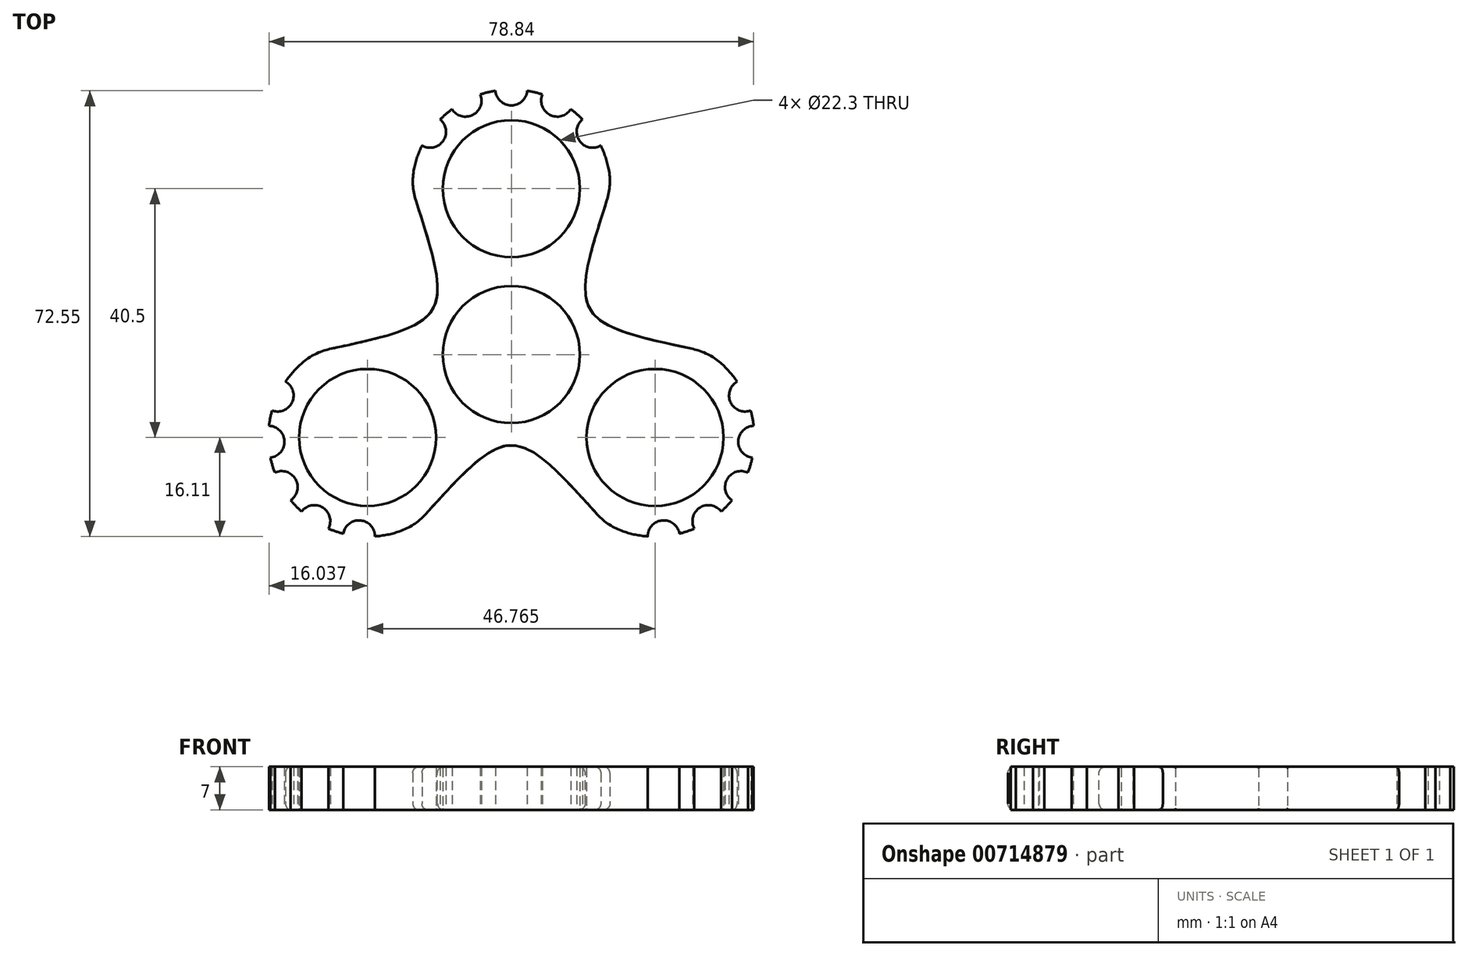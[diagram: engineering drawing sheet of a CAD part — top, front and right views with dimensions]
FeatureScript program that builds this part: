
annotation { "Feature Type Name" : "Feature", "Feature Type Description" : "" }
export const myFeature = defineFeature(function(context is Context, id is Id, definition is map)
    precondition{}
    {
        {
            var Q0;
            Q0=qCreatedBy(makeId("Top.planeOp"),FACE);
            var sketch = newSketch(context, id + "F0", { "sketchPlane" : qUnion([Q0])});
            skCircle(sketch, "E0", {"center": v(0, 0) * mm, "radius": 11.15 * mm});
            skLineSegment(sketch, "E1.0", {"start": v(-15.15, 0) * mm, "end": v(-15.15, 0) * mm});
            skLineSegment(sketch, "E2", {"start": v(0, 0) * mm, "end": v(0, 27) * mm, "construction": true});
            skCircle(sketch, "E3", {"center": v(0, 27) * mm, "radius": 11.15 * mm});
            skArc(sketch, "E4.0", {"start": v(16.15, 27) * mm, "mid": v(0, 43.15) * mm, "end": v(-16.15, 27) * mm});
            skLineSegment(sketch, "E5", {"start": v(-15.15, 0) * mm, "end": v(15.15, 0) * mm, "construction": true});
            skLineSegment(sketch, "E6", {"start": v(-16.15, 27) * mm, "end": v(16.15, 27) * mm, "construction": true});
            skPoint(sketch, "E7.trimOffspring.end.orphan", {"position": v(-15.15, 0) * mm});
            skLineSegment(sketch, "E8", {"start": v(-16.15, 27) * mm, "end": v(-16.15, 27) * mm});
            skArc(sketch, "E9.trimOffspring", {"start": v(-15.15, 0) * mm, "mid": v(0, -15.15) * mm, "end": v(15.15, 0) * mm, "construction": true});
            skLineSegment(sketch, "E10.trimOffspring", {"start": v(16.15, 27) * mm, "end": v(16.15, 27) * mm});
            skCircle(sketch, "E11", {"center": v(0, 43.15) * mm, "radius": 2.6 * mm});
            skCircle(sketch, "E12.1.0", {"center": v(7.46, 41.33) * mm, "radius": 2.6 * mm});
            skCircle(sketch, "E12.2.0", {"center": v(13.23, 36.26) * mm, "radius": 2.6 * mm});
            skLineSegment(sketch, "E12.anchor1", {"start": v(0, 27) * mm, "end": v(0, 43.15) * mm, "construction": true});
            skLineSegment(sketch, "E12.anchor2", {"start": v(0, 27) * mm, "end": v(13.23, 36.26) * mm, "construction": true});
            skCircle(sketch, "E13.MirrorC", {"center": v(-7.46, 41.33) * mm, "radius": 2.6 * mm});
            skCircle(sketch, "E14.MirrorC", {"center": v(-13.23, 36.26) * mm, "radius": 2.6 * mm});
            skLineSegment(sketch, "E15.1.0", {"start": v(7.57, -13.12) * mm, "end": v(-7.58, 13.12) * mm, "construction": true});
            skCircle(sketch, "E15.1.1", {"center": v(-38.02, -6.67) * mm, "radius": 2.6 * mm});
            skLineSegment(sketch, "E15.1.2", {"start": v(0, 0) * mm, "end": v(-23.38, -13.5) * mm, "construction": true});
            skLineSegment(sketch, "E15.1.3", {"start": v(-23.38, -13.5) * mm, "end": v(-38.02, -6.67) * mm, "construction": true});
            skLineSegment(sketch, "E15.1.4", {"start": v(-15.3, -27.49) * mm, "end": v(-31.46, 0.49) * mm, "construction": true});
            skCircle(sketch, "E15.1.5", {"center": v(-23.38, -13.5) * mm, "radius": 11.15 * mm});
            skCircle(sketch, "E15.1.6", {"center": v(-24.8, -29.59) * mm, "radius": 2.6 * mm});
            skCircle(sketch, "E15.1.7", {"center": v(-32.06, -27.12) * mm, "radius": 2.6 * mm});
            skLineSegment(sketch, "E15.1.8", {"start": v(-23.38, -13.5) * mm, "end": v(-37.37, -21.57) * mm, "construction": true});
            skPoint(sketch, "E15.1.9", {"position": v(7.57, -13.12) * mm});
            skCircle(sketch, "E15.1.11", {"center": v(-39.52, -14.2) * mm, "radius": 2.6 * mm});
            skCircle(sketch, "E15.1.13", {"center": v(-37.37, -21.57) * mm, "radius": 2.6 * mm});
            skArc(sketch, "E15.1.14", {"start": v(-31.46, 0.49) * mm, "mid": v(-37.37, -21.57) * mm, "end": v(-15.3, -27.49) * mm});
            skPoint(sketch, "E15.1.15", {"position": v(-23.38, -13.5) * mm});
            skLineSegment(sketch, "E15.2.0", {"start": v(7.57, 13.12) * mm, "end": v(-7.58, -13.12) * mm, "construction": true});
            skCircle(sketch, "E15.2.1", {"center": v(24.8, -29.59) * mm, "radius": 2.6 * mm});
            skLineSegment(sketch, "E15.2.2", {"start": v(0, 0) * mm, "end": v(23.38, -13.5) * mm, "construction": true});
            skLineSegment(sketch, "E15.2.3", {"start": v(23.38, -13.5) * mm, "end": v(24.8, -29.59) * mm, "construction": true});
            skLineSegment(sketch, "E15.2.4", {"start": v(31.46, 0.49) * mm, "end": v(15.3, -27.49) * mm, "construction": true});
            skCircle(sketch, "E15.2.5", {"center": v(23.38, -13.5) * mm, "radius": 11.15 * mm});
            skCircle(sketch, "E15.2.6", {"center": v(38.02, -6.67) * mm, "radius": 2.6 * mm});
            skCircle(sketch, "E15.2.7", {"center": v(39.52, -14.2) * mm, "radius": 2.6 * mm});
            skLineSegment(sketch, "E15.2.8", {"start": v(23.38, -13.5) * mm, "end": v(37.37, -21.57) * mm, "construction": true});
            skCircle(sketch, "E15.2.11", {"center": v(32.06, -27.12) * mm, "radius": 2.6 * mm});
            skArc(sketch, "E15.2.12", {"start": v(7.57, 13.12) * mm, "mid": v(-13.12, 7.57) * mm, "end": v(-7.58, -13.12) * mm, "construction": true});
            skCircle(sketch, "E15.2.13", {"center": v(37.37, -21.57) * mm, "radius": 2.6 * mm});
            skArc(sketch, "E15.2.14", {"start": v(15.3, -27.49) * mm, "mid": v(37.37, -21.57) * mm, "end": v(31.46, 0.49) * mm});
            skPoint(sketch, "E15.2.15", {"position": v(23.38, -13.5) * mm});
            skFitSpline(sketch, "E16", {"points": [v(16.15, 27) * mm, v(31.46, 0.49) * mm], "startDerivative": vector(-21.08, -65.2) * mm, "endDerivative": vector(67, -14.34) * mm});
            skLineSegment(sketch, "E17", {"start": v(0, 0) * mm, "end": v(26.97, 15.57) * mm, "construction": true});
            skLineSegment(sketch, "E18", {"start": v(-15.3, -27.49) * mm, "end": v(-3.01, -11.46) * mm});
            skLineSegment(sketch, "E19", {"start": v(-3.01, -11.46) * mm, "end": v(3.36, -11.46) * mm});
            skLineSegment(sketch, "E20", {"start": v(3.36, -11.46) * mm, "end": v(15.3, -27.49) * mm});
            skLineSegment(sketch, "E21", {"start": v(-31.46, 0.49) * mm, "end": v(-13.47, 2.14) * mm});
            skLineSegment(sketch, "E22", {"start": v(-13.47, 2.14) * mm, "end": v(-9.18, 9.2) * mm});
            skLineSegment(sketch, "E23", {"start": v(-9.18, 9.2) * mm, "end": v(-16.15, 27) * mm});
            skSolve(sketch);
        }
        {
            var Q0;
            Q0=qCreatedBy(makeId("Right.planeOp"),FACE);
            var sketch = newSketch(context, id + "F1", { "sketchPlane" : qUnion([Q0])});
            skLineSegment(sketch, "E24", {"start": v(0, 18.91) * mm, "end": v(0, -18.72) * mm, "construction": true});
            skSolve(sketch);
        }
        {
            var Q0;
            Q0=makeQuery(id+"F0.imprint","IMPRINT",FACE,{"disambiguationData":[TD([[makeQuery(id+"F0.imprint","IMPRINT",EDGE,{"derivedFrom":sQuery(id+"F0.wireOp",EDGE,"E0")}),-1.0]])]});
            var Q1;
            Q1=makeQuery(id+"F0.imprint","IMPRINT",FACE,{"disambiguationData":[TD([[makeQuery(id+"F0.imprint","IMPRINT",EDGE,{"derivedFrom":sQuery(id+"F0.wireOp",EDGE,"E3")}),-1.0]])]});
            extrude(context, id + "F2", {"entities" : qUnion([Q0, Q1]), "depth" : 7 * mm, "offsetDistance" : 25 * mm});
        }
        {
            var Q0;
            Q0=makeQuery(id+"F2.opExtrude","SWEPT_BODY",BODY,{"disambiguationData":[OSD([sQuery(id+"F0.wireOp",EDGE,"E0"),sQuery(id+"F0.wireOp",EDGE,"E1.0"),sQuery(id+"F0.wireOp",EDGE,"E3"),sQuery(id+"F0.wireOp",EDGE,"E4.0"),sQuery(id+"F0.wireOp",EDGE,"oIW5whhO-fQ4n-saJ2-gWf4-q0JPziCMkqRt"),sQuery(id+"F0.wireOp",EDGE,"e7664bf7-e720-472f-93c8-efa73fce652a0.MirrorCS"),sQuery(id+"F0.wireOp",EDGE,"15db0cb3-5bd8-46cc-a881-ea2e00802e11.filletArc"),sQuery(id+"F0.wireOp",EDGE,"163ba6b5-26b9-4c58-8659-ca6763b85cf9.filletArc")])]});
            var Q1;
            Q1=sQuery(id+"F1.wireOp",EDGE,"E24");
            circularPattern(context, id + "F3", {"operationType" : NewBodyOperationType.ADD, "entities" : qUnion([Q0]), "axis" : qUnion([Q1]), "angle" : 360 * degree, "instanceCount" : 3, "equalSpace" : true});
        }
        {
            var Q0;
            Q0=makeQuery(id+"F2.opExtrude","SWEPT_EDGE",EDGE,{"disambiguationData":[OSD([sQuery(id+"F0.wireOp",EDGE,"E4.0"),sQuery(id+"F0.wireOp",EDGE,"E16")])]});
            var Q1;
            Q1=makeQuery(id+"F2.opExtrude","SWEPT_EDGE",EDGE,{"disambiguationData":[OSD([sQuery(id+"F0.wireOp",EDGE,"E15.2.14"),sQuery(id+"F0.wireOp",EDGE,"E16")])]});
            var Q2;
            Q2=makeQuery(id+"F3.boolean.opBoolean","MERGE",EDGE,{"derivedFrom":[makeQuery(id+"F2.opExtrude","SWEPT_EDGE",EDGE,{"disambiguationData":[OSD([sQuery(id+"F0.wireOp",EDGE,"E15.2.14"),sQuery(id+"F0.wireOp",EDGE,"E20")])]}),makeQuery(id+"F3.opPattern","COPY",EDGE,{"derivedFrom":makeQuery(id+"F2.opExtrude","SWEPT_EDGE",EDGE,{"disambiguationData":[OSD([sQuery(id+"F0.wireOp",EDGE,"E4.0"),sQuery(id+"F0.wireOp",EDGE,"E16")])]}),"instanceName":"1"})]});
            var Q3;
            Q3=makeQuery(id+"F3.boolean.opBoolean","MERGE",EDGE,{"derivedFrom":[makeQuery(id+"F2.opExtrude","SWEPT_EDGE",EDGE,{"disambiguationData":[OSD([sQuery(id+"F0.wireOp",EDGE,"E15.1.14"),sQuery(id+"F0.wireOp",EDGE,"E18")])]}),makeQuery(id+"F3.opPattern","COPY",EDGE,{"derivedFrom":makeQuery(id+"F2.opExtrude","SWEPT_EDGE",EDGE,{"disambiguationData":[OSD([sQuery(id+"F0.wireOp",EDGE,"E15.2.14"),sQuery(id+"F0.wireOp",EDGE,"E16")])]}),"instanceName":"1"})]});
            var Q4;
            Q4=makeQuery(id+"F3.boolean.opBoolean","MERGE",EDGE,{"derivedFrom":[makeQuery(id+"F2.opExtrude","SWEPT_EDGE",EDGE,{"disambiguationData":[OSD([sQuery(id+"F0.wireOp",EDGE,"E15.1.14"),sQuery(id+"F0.wireOp",EDGE,"E21")])]}),makeQuery(id+"F3.opPattern","COPY",EDGE,{"derivedFrom":makeQuery(id+"F2.opExtrude","SWEPT_EDGE",EDGE,{"disambiguationData":[OSD([sQuery(id+"F0.wireOp",EDGE,"E15.2.14"),sQuery(id+"F0.wireOp",EDGE,"E20")])]}),"instanceName":"1"}),makeQuery(id+"F3.opPattern","COPY",EDGE,{"derivedFrom":makeQuery(id+"F2.opExtrude","SWEPT_EDGE",EDGE,{"disambiguationData":[OSD([sQuery(id+"F0.wireOp",EDGE,"E4.0"),sQuery(id+"F0.wireOp",EDGE,"E16")])]}),"instanceName":"2"})]});
            var Q5;
            Q5=makeQuery(id+"F3.boolean.opBoolean","MERGE",EDGE,{"derivedFrom":[makeQuery(id+"F2.opExtrude","SWEPT_EDGE",EDGE,{"disambiguationData":[OSD([sQuery(id+"F0.wireOp",EDGE,"E4.0"),sQuery(id+"F0.wireOp",EDGE,"E23")])]}),makeQuery(id+"F3.opPattern","COPY",EDGE,{"derivedFrom":makeQuery(id+"F2.opExtrude","SWEPT_EDGE",EDGE,{"disambiguationData":[OSD([sQuery(id+"F0.wireOp",EDGE,"E15.1.14"),sQuery(id+"F0.wireOp",EDGE,"E18")])]}),"instanceName":"1"}),makeQuery(id+"F3.opPattern","COPY",EDGE,{"derivedFrom":makeQuery(id+"F2.opExtrude","SWEPT_EDGE",EDGE,{"disambiguationData":[OSD([sQuery(id+"F0.wireOp",EDGE,"E15.2.14"),sQuery(id+"F0.wireOp",EDGE,"E16")])]}),"instanceName":"2"})]});
            fillet(context, id + "F4", {"entities" : qUnion([Q0, Q1, Q2, Q3, Q4, Q5]), "radius" : 10 * mm, "tangentPropagation" : true, "allowEdgeOverflow" : false});
        }
        {
            var Q0;
            Q0=makeQuery(id+"F2.opExtrude","CAP_EDGE",EDGE,{"disambiguationData":[OSD([sQuery(id+"F0.wireOp",EDGE,"E16")])],"isStart":false});
            var Q1;
            Q1=makeQuery(id+"F3.opPattern","COPY",EDGE,{"derivedFrom":makeQuery(id+"F2.opExtrude","CAP_EDGE",EDGE,{"disambiguationData":[OSD([sQuery(id+"F0.wireOp",EDGE,"E16")])],"isStart":false}),"instanceName":"2"});
            var Q2;
            Q2=makeQuery(id+"F3.opPattern","COPY",EDGE,{"derivedFrom":makeQuery(id+"F2.opExtrude","CAP_EDGE",EDGE,{"disambiguationData":[OSD([sQuery(id+"F0.wireOp",EDGE,"E16")])],"isStart":false}),"instanceName":"1"});
            var Q3;
            Q3=makeQuery(id+"F3.opPattern","COPY",EDGE,{"derivedFrom":makeQuery(id+"F2.opExtrude","CAP_EDGE",EDGE,{"disambiguationData":[OSD([sQuery(id+"F0.wireOp",EDGE,"E16")])],"isStart":true}),"instanceName":"1"});
            var Q4;
            Q4=makeQuery(id+"F3.opPattern","COPY",EDGE,{"derivedFrom":makeQuery(id+"F2.opExtrude","CAP_EDGE",EDGE,{"disambiguationData":[OSD([sQuery(id+"F0.wireOp",EDGE,"E16")])],"isStart":true}),"instanceName":"2"});
            var Q5;
            Q5=makeQuery(id+"F2.opExtrude","CAP_EDGE",EDGE,{"disambiguationData":[OSD([sQuery(id+"F0.wireOp",EDGE,"E16")])],"isStart":true});
            fillet(context, id + "F5", {"entities" : qUnion([Q0, Q1, Q2, Q3, Q4, Q5]), "radius" : 1 * mm, "tangentPropagation" : true, "allowEdgeOverflow" : false});
        }
        {
            var Q0;
            Q0=makeQuery(id+"F2.opExtrude","SWEPT_FACE",FACE,{"disambiguationData":[OSD([sQuery(id+"F0.wireOp",EDGE,"E0")])]});
            var Q1;
            Q1=makeQuery(id+"F2.opExtrude","SWEPT_FACE",FACE,{"disambiguationData":[OSD([sQuery(id+"F0.wireOp",EDGE,"E15.2.5")])]});
            var Q2;
            Q2=makeQuery(id+"F2.opExtrude","SWEPT_FACE",FACE,{"disambiguationData":[OSD([sQuery(id+"F0.wireOp",EDGE,"E15.1.5")])]});
            var Q3;
            Q3=makeQuery(id+"F2.opExtrude","SWEPT_FACE",FACE,{"disambiguationData":[OSD([sQuery(id+"F0.wireOp",EDGE,"E3")])]});
            fillet(context, id + "F6", {"entities" : qUnion([Q0, Q1, Q2, Q3]), "radius" : 0.2 * mm, "tangentPropagation" : true, "allowEdgeOverflow" : false});
        }
    });
